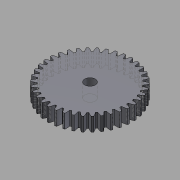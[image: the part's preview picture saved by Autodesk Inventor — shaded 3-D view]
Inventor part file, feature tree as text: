
AUTODESK INVENTOR PART (.ipt)
format: ipt  version: 2015 (Build 190159000, 159)  size: 302,080 bytes
history: native  units: mm (DEFAULTED — no unit token found)
features: plane x3, other x3, sketch x3, extrude x2
ambient origin geometry x8: Origin, YZ Plane, XZ Plane, XY Plane, X Axis, Y Axis, Z Axis, Center Point
bodies: Solid1 (feature_tree)
feature tree (11):
  extrude  "Extrusion1"  Depth=3.3mm TaperAngle=0.0deg
  plane  "Work Plane2"
  plane  "Work Plane8"
  plane  "Work Plane9"
  other  "Spur Gear"
  extrude  "Extrusion2"  Depth=10.0mm TaperAngle=0.0deg
  sketch  "Sketch1"  dims[d0=20.0mm d1=3.3mm d2=0.0mm]
  sketch  "Sketch2"  dims[d3=19.0mm d4=10.0mm d5=0.0mm]
  other  "Srf1"
  sketch  "Sketch3"  dims[d16=12.0mm d17=0.0mm d34=0.826735mm d39=0.0mm d41=0.0mm d43=12.0mm d46=12.0mm d47=0.0mm d48=0.0mm d49=2.5mm d50=10.0mm d51=0.0mm]
  other  "Pitch Diameter"
